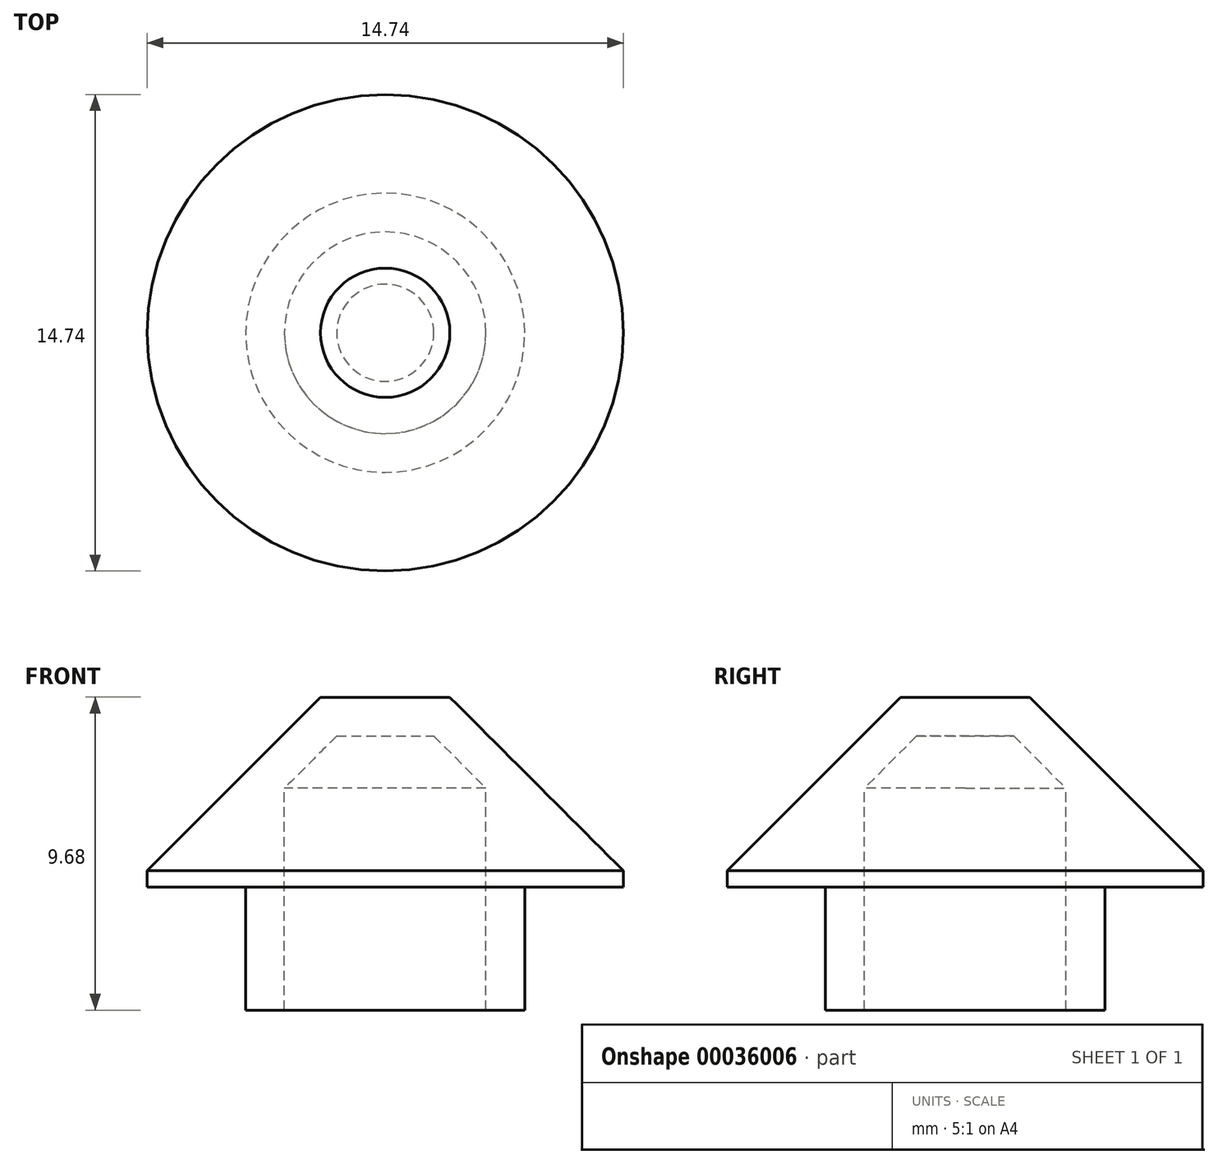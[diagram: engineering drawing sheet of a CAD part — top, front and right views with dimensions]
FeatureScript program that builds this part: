
annotation { "Feature Type Name" : "Feature", "Feature Type Description" : "" }
export const myFeature = defineFeature(function(context is Context, id is Id, definition is map)
    precondition{}
    {
        {
            var Q0;
            Q0=qCreatedBy(makeId("Front.planeOp"),FACE);
            var sketch = newSketch(context, id + "F0", { "sketchPlane" : qUnion([Q0])});
            skLineSegment(sketch, "E0", {"start": v(0, 0) * mm, "end": v(4.32, 0) * mm});
            skLineSegment(sketch, "E1", {"start": v(4.32, 0) * mm, "end": v(4.32, 3.81) * mm});
            skLineSegment(sketch, "E2", {"start": v(4.32, 3.81) * mm, "end": v(7.37, 3.81) * mm});
            skLineSegment(sketch, "E3", {"start": v(7.37, 3.81) * mm, "end": v(7.37, 4.3) * mm});
            skLineSegment(sketch, "E4", {"start": v(7.37, 4.3) * mm, "end": v(2, 9.68) * mm});
            skLineSegment(sketch, "E5", {"start": v(2, 9.68) * mm, "end": v(0, 9.68) * mm});
            skLineSegment(sketch, "E6", {"start": v(0, 9.68) * mm, "end": v(0, 0) * mm});
            skSolve(sketch);
        }
        {
            var Q0;
            Q0=makeQuery(id+"F0.imprint","IMPRINT",FACE,{"disambiguationData":[TD([[makeQuery(id+"F0.imprint","IMPRINT",EDGE,{"derivedFrom":sQuery(id+"F0.wireOp",EDGE,"E0")}),1.0]])]});
            var Q1;
            Q1=sQuery(id+"F0.wireOp",EDGE,"E6");
            revolve(context, id + "F1", {"entities" : qUnion([Q0]), "axis" : qUnion([Q1]), "revolveType" : RevolveType.FULL});
        }
        {
            var Q0;
            Q0=makeQuery(id+"F1.opRevolve","SWEPT_FACE",FACE,{"disambiguationData":[OSD([sQuery(id+"F0.wireOp",EDGE,"E0")])]});
            shell(context, id + "F2", {"entities" : qUnion([Q0]), "thickness" : 1.2 * mm});
        }
        {
            var Q0;
            Q0=qCreatedBy(makeId("Front.planeOp"),FACE);
            var sketch = newSketch(context, id + "F3", { "sketchPlane" : qUnion([Q0])});
            skLineSegment(sketch, "E7", {"start": v(3.12, 6.86) * mm, "end": v(4.97, 5) * mm});
            skLineSegment(sketch, "E8", {"start": v(3.12, 6.86) * mm, "end": v(3.12, 5) * mm});
            skLineSegment(sketch, "E9.trimOffspring", {"start": v(3.12, 5) * mm, "end": v(4.97, 5) * mm});
            skSolve(sketch);
        }
        {
            var Q0;
            Q0=makeQuery(id+"F3.imprint","IMPRINT",FACE,{"disambiguationData":[TD([[makeQuery(id+"F3.imprint","IMPRINT",EDGE,{"derivedFrom":sQuery(id+"F3.wireOp",EDGE,"E7")}),-1.0]])]});
            var Q1;
            Q1=makeQuery(id+"F2.opShell","OFFSET_FACE",FACE,{"disambiguationData":[OSD([sQuery(id+"F0.wireOp",EDGE,"E1")])]});
            revolve(context, id + "F4", {"operationType" : NewBodyOperationType.ADD, "entities" : qUnion([Q0]), "axis" : qUnion([Q1]), "revolveType" : RevolveType.FULL});
        }
    });
